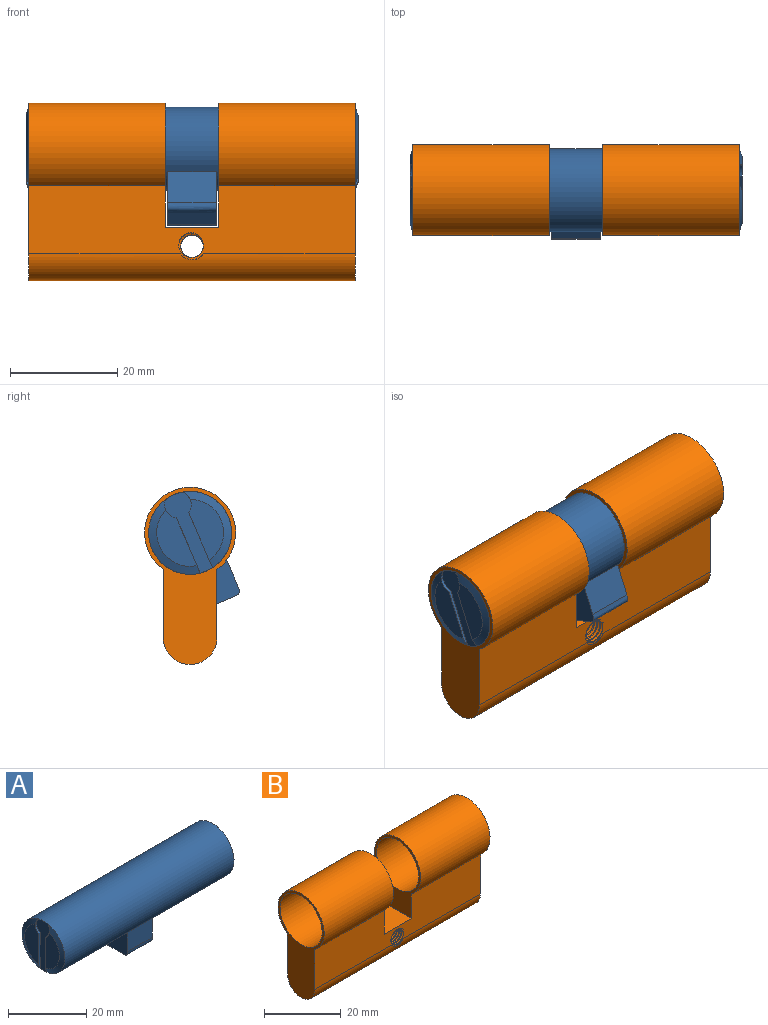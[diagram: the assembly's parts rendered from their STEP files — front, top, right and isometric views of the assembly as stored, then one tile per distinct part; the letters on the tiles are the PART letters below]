
ASSEMBLY  parts=2 mates=1
PART A: 26 faces, bbox 62.3x15.8x22.3 mm
  f0: cylinder r=7.75mm len=61mm, axis (-1,0,0), area 2889.4mm2, adj f3,f4,f5,f7,f12,f17,f22,f23
  f1: plane 11.85x5mm, normal (-1,0,0), area 43.7mm2, adj f18,f19,f24
  f2: plane 11.85x5mm, normal (1,0,0), area 43.7mm2, adj f13,f14,f23
  f3: plane 9x6.21mm, normal (0,1,0), area 55.9mm2, adj f0,f5,f7,f11
  f4: plane 9x6.21mm, normal (0,-1,0), area 55.9mm2, adj f0,f5,f7,f10
  f5: plane 8.81x8.02mm, normal (-1,0,0), area 57.6mm2, adj f0,f3,f4,f6,f10,f11
  f6: plane 9x5.5mm, normal (0,0,-1), area 49.5mm2, adj f5,f7,f10,f11
  f7: plane 8.81x8.02mm, normal (1,0,0), area 57.6mm2, adj f0,f3,f4,f6,f10,f11
  f8: plane 11.85x5mm, normal (1,0,0), area 43.7mm2, adj f15,f16,f22
  f9: plane 11.85x5mm, normal (-1,0,0), area 43.7mm2, adj f20,f21,f25
  f10: bspline ~9.9x1.5mm, area 22.8mm2, adj f4,f5,f6,f7
  f11: bspline ~9.9x1.5mm, area 22.8mm2, adj f3,f5,f6,f7
  f12: plane 15.5x5mm, normal (1,0,0), area 46.1mm2, adj f0,f13,f14,f15,f16
  f13: plane 11.26x0.53mm, normal (0,-1,0), area 5.2mm2, adj f2,f12,f14,f23
  f14: cylinder r=2.5mm len=3.97mm, axis (1,0,0), area 1.8mm2, adj f2,f12,f13,f23
  f15: cylinder r=2.5mm len=3.97mm, axis (1,0,0), area 1.8mm2, adj f8,f12,f16,f22
  f16: plane 11.26x0.53mm, normal (0,1,0), area 5.2mm2, adj f8,f12,f15,f22
  f17: plane 15.5x5mm, normal (-1,0,0), area 46.1mm2, adj f0,f18,f19,f20,f21
  f18: plane 11.26x0.53mm, normal (0,1,0), area 5.2mm2, adj f1,f17,f19,f24
  f19: cylinder r=2.5mm len=3.97mm, axis (-1,0,0), area 1.8mm2, adj f1,f17,f18,f24
  f20: plane 11.26x0.53mm, normal (0,-1,0), area 5.2mm2, adj f9,f17,f21,f25
  f21: cylinder r=2.5mm len=3.97mm, axis (-1,0,0), area 1.8mm2, adj f9,f17,f20,f25
  f22: cone r=6.25mm half-angle=71.6deg, axis (-1,0,0), area 29.3mm2, adj f0,f8,f15,f16
  f23: cone r=6.25mm half-angle=71.6deg, axis (-1,0,0), area 29.3mm2, adj f0,f2,f13,f14
  f24: cone r=7.75mm half-angle=71.6deg, axis (1,0,0), area 29.3mm2, adj f0,f1,f18,f19
  f25: cone r=7.75mm half-angle=71.6deg, axis (1,0,0), area 29.3mm2, adj f0,f9,f20,f21
PART B: 18 faces, bbox 61.2x17.2x33.3 mm
  f0: cylinder r=5mm len=61mm, axis (-1,0,0), area 951.4mm2, adj f1,f4,f5,f6,f12,f15,f16
  f1: plane 61.23x14.1mm, normal (0,1,0), area 685mm2, adj f0,f2,f3,f5,f6,f7,f8,f9
  f2: cylinder r=8.5mm len=25.5mm, axis (-1,0,0), area 1089.3mm2, adj f1,f4,f6,f7
  f3: cylinder r=8.5mm len=25.5mm, axis (-1,0,0), area 1089.3mm2, adj f1,f4,f5,f9
  f4: plane 61.23x14.1mm, normal (0,-1,0), area 685mm2, adj f0,f2,f3,f5,f6,f7,f8,f9
  f5: plane 33.1x17mm, normal (1,0,0), area 193.8mm2, adj f0,f1,f3,f4,f10
  f6: plane 33.1x17mm, normal (-1,0,0), area 193.8mm2, adj f0,f1,f2,f4,f11
  f7: plane 23.19x17mm, normal (1,0,0), area 105.4mm2, adj f1,f2,f4,f8,f11
  f8: plane 10x10mm, normal (0,0,1), area 100mm2, adj f1,f4,f7,f9
  f9: plane 23.19x17mm, normal (-1,0,0), area 105.4mm2, adj f1,f3,f4,f8,f10
  f10: cylinder r=7.75mm len=25.5mm, axis (-1,0,0), area 1241.7mm2, adj f5,f9
  f11: cylinder r=7.75mm len=25.5mm, axis (-1,0,0), area 1241.7mm2, adj f6,f7
  f12: bspline ~10.37x5.93mm, area 23.2mm2, adj f0,f1,f4,f13,f14,f16
  f13: bspline ~10.52x5.85mm, area 91.3mm2, adj f1,f4,f12,f17
  f14: bspline ~10.65x5.85mm, area 90.9mm2, adj f1,f4,f12,f17
  f15: cylinder r=2.55mm len=4.25mm, axis (0,-1,0), area 0mm2, adj f0,f4
  f16: cylinder r=2.55mm len=3.82mm, axis (0,-1,0), area 0mm2, adj f0,f1,f12
  f17: cylinder r=2.1mm len=10mm, axis (0,-1,0), area 24.1mm2, adj f1,f4,f13,f14
PLACE A rot(axis=(-1,0,0),23.4deg) t=(-18.54,-9.34,4.81)mm
PLACE B t=(-18.54,0.43,2.79)mm fixed
MATE revolute A.f0 <-> B.f2  axis (-1,0,0) through (-18.54,0.43,27.39)mm
